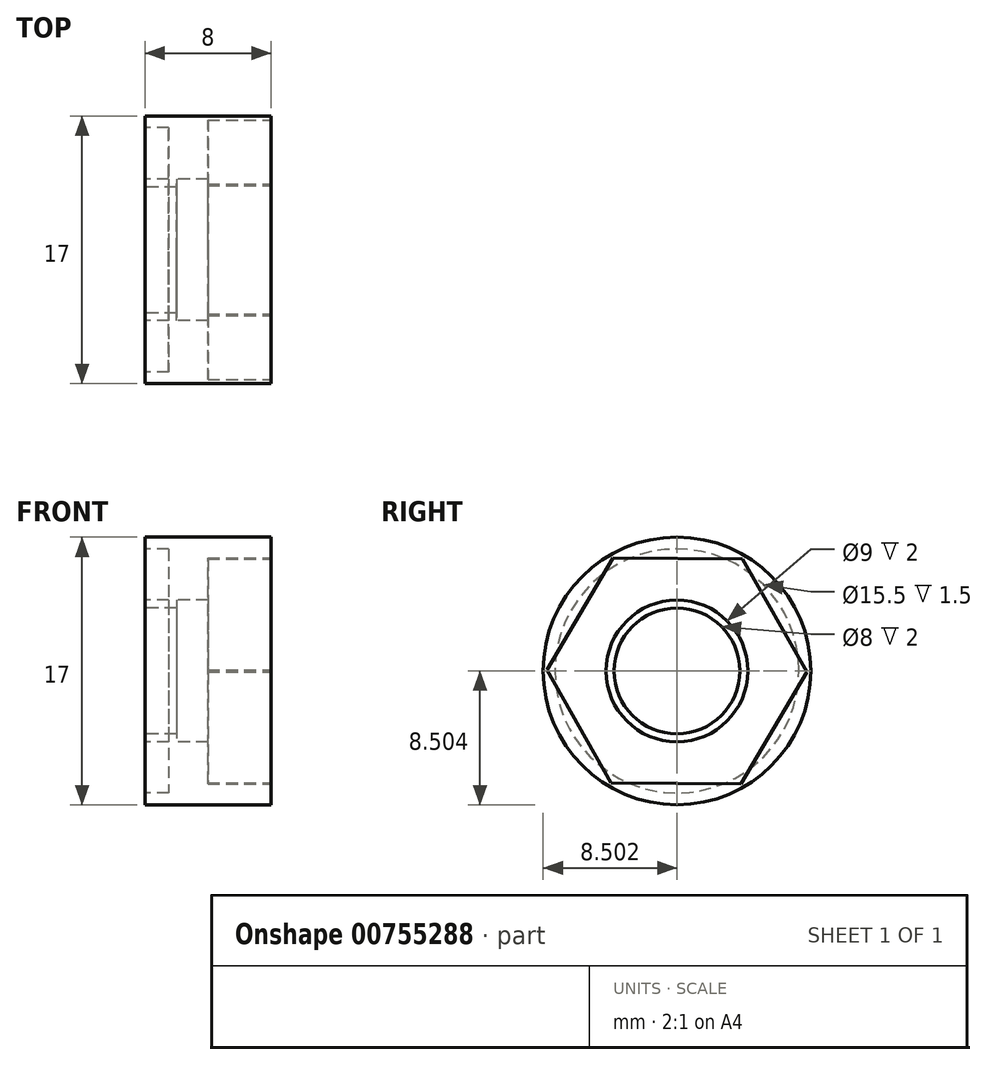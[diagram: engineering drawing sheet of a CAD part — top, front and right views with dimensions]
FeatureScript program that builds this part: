
annotation { "Feature Type Name" : "Feature", "Feature Type Description" : "" }
export const myFeature = defineFeature(function(context is Context, id is Id, definition is map)
    precondition{}
    {
        {
            var Q0;
            Q0=qCreatedBy(makeId("Right.planeOp"),FACE);
            var sketch = newSketch(context, id + "F0", { "sketchPlane" : qUnion([Q0])});
            skCircle(sketch, "E0", {"center": v(-39, 9.35) * mm, "radius": 8.5 * mm});
            skSolve(sketch);
        }
        {
            var Q0;
            Q0=makeQuery(id+"F0.imprint","IMPRINT",FACE,{"disambiguationData":[TD([[makeQuery(id+"F0.imprint","IMPRINT",EDGE,{"derivedFrom":sQuery(id+"F0.wireOp",EDGE,"E0")}),1.0]])]});
            extrude(context, id + "F1", {"entities" : qUnion([Q0]), "depth" : 8 * mm, "offsetDistance" : 25 * mm});
        }
        {
            var Q0;
            Q0=makeQuery(id+"F1.opExtrude","CAP_FACE",FACE,{"disambiguationData":[OSD([sQuery(id+"F0.wireOp",EDGE,"E0")])],"isStart":false});
            var sketch = newSketch(context, id + "F2", { "sketchPlane" : qUnion([Q0])});
            skLineSegment(sketch, "E1.0", {"start": v(-43.07, 16.53) * mm, "end": v(-34.82, 16.47) * mm});
            skLineSegment(sketch, "E1.1", {"start": v(-34.82, 16.47) * mm, "end": v(-30.75, 9.3) * mm});
            skLineSegment(sketch, "E1.2", {"start": v(-30.75, 9.3) * mm, "end": v(-34.92, 2.18) * mm});
            skLineSegment(sketch, "E1.3", {"start": v(-34.92, 2.18) * mm, "end": v(-43.17, 2.24) * mm});
            skLineSegment(sketch, "E1.4", {"start": v(-43.17, 2.24) * mm, "end": v(-47.25, 9.41) * mm});
            skLineSegment(sketch, "E1.5", {"start": v(-47.25, 9.41) * mm, "end": v(-43.07, 16.53) * mm});
            skSolve(sketch);
        }
        {
            var Q0;
            Q0=makeQuery(id+"F2.imprint","IMPRINT",FACE,{"disambiguationData":[TD([[makeQuery(id+"F2.imprint","IMPRINT",EDGE,{"derivedFrom":sQuery(id+"F2.wireOp",EDGE,"E1.0")}),-1.0]])]});
            extrude(context, id + "F3", {"entities" : qUnion([Q0]), "operationType" : NewBodyOperationType.REMOVE, "oppositeDirection" : true, "depth" : 4 * mm, "offsetDistance" : 25 * mm});
        }
        {
            var Q0;
            Q0=makeQuery(id+"F1.opExtrude","CAP_FACE",FACE,{"disambiguationData":[OSD([sQuery(id+"F0.wireOp",EDGE,"E0")])],"isStart":true});
            var sketch = newSketch(context, id + "F4", { "sketchPlane" : qUnion([Q0])});
            skCircle(sketch, "E2", {"center": v(39, 9.35) * mm, "radius": 7.75 * mm});
            skSolve(sketch);
        }
        {
            var Q0;
            Q0=makeQuery(id+"F4.imprint","IMPRINT",FACE,{"disambiguationData":[TD([[makeQuery(id+"F4.imprint","IMPRINT",EDGE,{"derivedFrom":sQuery(id+"F4.wireOp",EDGE,"E2")}),1.0]])]});
            extrude(context, id + "F5", {"entities" : qUnion([Q0]), "operationType" : NewBodyOperationType.REMOVE, "oppositeDirection" : true, "depth" : 1.5 * mm, "offsetDistance" : 25 * mm});
        }
        {
            var Q0;
            Q0=makeQuery(id+"F1.opExtrude","CAP_FACE",FACE,{"disambiguationData":[OSD([sQuery(id+"F0.wireOp",EDGE,"E0")])],"isStart":true});
            var sketch = newSketch(context, id + "F6", { "sketchPlane" : qUnion([Q0])});
            skCircle(sketch, "E3", {"center": v(39, 9.35) * mm, "radius": 4.5 * mm});
            skSolve(sketch);
        }
        {
            var Q0;
            Q0=makeQuery(id+"F6.imprint","IMPRINT",FACE,{"disambiguationData":[TD([[makeQuery(id+"F6.imprint","IMPRINT",EDGE,{"derivedFrom":sQuery(id+"F6.wireOp",EDGE,"E3")}),1.0]])]});
            var sketch = newSketch(context, id + "F7", { "sketchPlane" : qUnion([Q0])});
            skSolve(sketch);
        }
        {
            var Q0;
            Q0=qSketchRegion(id+"F7",true);
            var Q1;
            Q1=makeQuery(id+"F7.imprint","IMPRINT",FACE,{"disambiguationData":[TD([[makeQuery(id+"F7.imprint","IMPRINT",EDGE,{"derivedFrom":makeQuery(id+"F6.imprint","IMPRINT",EDGE,{"derivedFrom":sQuery(id+"F6.wireOp",EDGE,"E3")})}),1.0]])]});
            extrude(context, id + "F8", {"entities" : qUnion([Q0, Q1]), "operationType" : NewBodyOperationType.REMOVE, "oppositeDirection" : true, "depth" : 25 * mm, "offsetDistance" : 25 * mm});
        }
        {
            var Q0;
            Q0=makeQuery(id+"F6.imprint","IMPRINT",FACE,{"disambiguationData":[TD([[makeQuery(id+"F6.imprint","IMPRINT",EDGE,{"derivedFrom":sQuery(id+"F6.wireOp",EDGE,"E3")}),1.0]])]});
            extrude(context, id + "F9", {"entities" : qUnion([Q0]), "operationType" : NewBodyOperationType.ADD, "oppositeDirection" : true, "depth" : 2 * mm, "offsetDistance" : 25 * mm});
        }
        {
            var Q0;
            Q0=makeQuery(id+"F9.opExtrude","CAP_FACE",FACE,{"disambiguationData":[OSD([sQuery(id+"F6.wireOp",EDGE,"E3")])],"isStart":true});
            var sketch = newSketch(context, id + "F10", { "sketchPlane" : qUnion([Q0])});
            skCircle(sketch, "E4", {"center": v(39, 9.35) * mm, "radius": 4 * mm});
            skSolve(sketch);
        }
        {
            var Q0;
            Q0=makeQuery(id+"F10.imprint","IMPRINT",FACE,{"disambiguationData":[TD([[makeQuery(id+"F10.imprint","IMPRINT",EDGE,{"derivedFrom":sQuery(id+"F10.wireOp",EDGE,"E4")}),1.0]])]});
            extrude(context, id + "F11", {"entities" : qUnion([Q0]), "operationType" : NewBodyOperationType.REMOVE, "oppositeDirection" : true, "depth" : 10 * mm, "offsetDistance" : 25 * mm});
        }
    });
